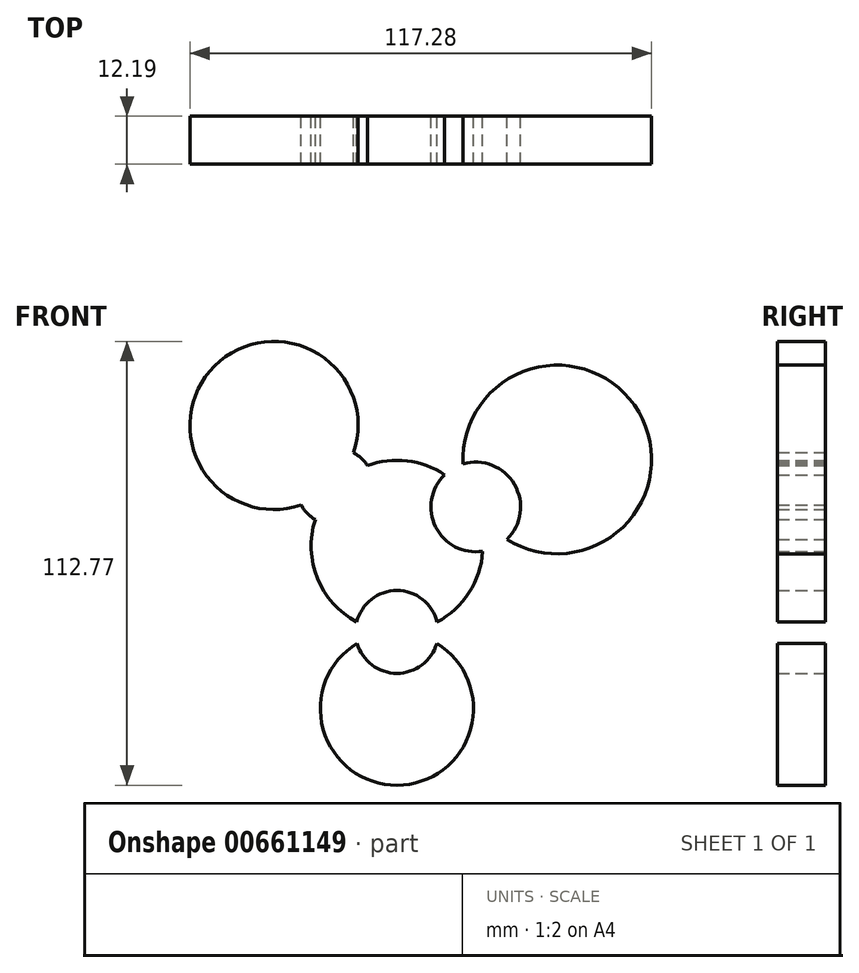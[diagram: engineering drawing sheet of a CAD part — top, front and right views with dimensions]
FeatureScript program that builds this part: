
annotation { "Feature Type Name" : "Feature", "Feature Type Description" : "" }
export const myFeature = defineFeature(function(context is Context, id is Id, definition is map)
    precondition{}
    {
        {
            var Q0;
            Q0=qCreatedBy(makeId("Front.planeOp"),FACE);
            var sketch = newSketch(context, id + "F0", { "sketchPlane" : qUnion([Q0])});
            skCircle(sketch, "E0", {"center": v(0, 0) * mm, "radius": 21.8 * mm});
            skCircle(sketch, "E1", {"center": v(-31.23, 30.65) * mm, "radius": 21.37 * mm});
            skCircle(sketch, "E2", {"center": v(40.72, 22.02) * mm, "radius": 23.96 * mm});
            skCircle(sketch, "E3", {"center": v(0, -41.3) * mm, "radius": 19.45 * mm});
            skCircle(sketch, "E4", {"center": v(-15.7, 15.13) * mm, "radius": 9.8 * mm});
            skCircle(sketch, "E5", {"center": v(20.03, 9.94) * mm, "radius": 11.38 * mm});
            skCircle(sketch, "E6", {"center": v(0, -21.8) * mm, "radius": 10.52 * mm});
            skCircle(sketch, "E7", {"center": v(-31.23, 30.65) * mm, "radius": 10.65 * mm});
            skCircle(sketch, "E8", {"center": v(40.72, 22.02) * mm, "radius": 11.28 * mm});
            skCircle(sketch, "E9", {"center": v(0, -41.3) * mm, "radius": 7.89 * mm});
            skSolve(sketch);
        }
        {
            var Q0;
            Q0=makeQuery(id+"F0.imprint","IMPRINT",FACE,{"disambiguationData":[TD([[makeQuery(id+"F0.imprint","IMPRINT",EDGE,{"derivedFrom":sQuery(id+"F0.wireOp",EDGE,"E9")}),1.0]])]});
            var Q1;
            {var subQ0=sQuery(id+"F0.wireOp",EDGE,"E6");var subQ1=sQuery(id+"F0.wireOp",EDGE,"E3");var subQ2=makeQuery(id+"F0.imprint","INTERSECT",VERTEX,{"disambiguationData":[OD(0.0)],"derivedFrom":[subQ1,subQ0]});Q1=makeQuery(id+"F0.imprint","IMPRINT",FACE,{"disambiguationData":[TD([[makeQuery(id+"F0.imprint","IMPRINT",EDGE,{"disambiguationData":[TD([[subQ2,1.0]])],"derivedFrom":subQ1}),1.0]])]});}
            var Q2;
            Q2=makeQuery(id+"F0.imprint","IMPRINT",FACE,{"disambiguationData":[TD([[makeQuery(id+"F0.imprint","IMPRINT",EDGE,{"derivedFrom":sQuery(id+"F0.wireOp",EDGE,"E8")}),1.0]])]});
            var Q3;
            Q3=makeQuery(id+"F0.imprint","IMPRINT",FACE,{"disambiguationData":[TD([[makeQuery(id+"F0.imprint","IMPRINT",EDGE,{"derivedFrom":sQuery(id+"F0.wireOp",EDGE,"E9")}),-1.0]])]});
            var Q4;
            {var subQ0=sQuery(id+"F0.wireOp",EDGE,"E6");var subQ1=sQuery(id+"F0.wireOp",EDGE,"E0");var subQ2=makeQuery(id+"F0.imprint","INTERSECT",VERTEX,{"disambiguationData":[OD(0.0)],"derivedFrom":[subQ1,subQ0]});Q4=makeQuery(id+"F0.imprint","IMPRINT",FACE,{"disambiguationData":[TD([[makeQuery(id+"F0.imprint","IMPRINT",EDGE,{"disambiguationData":[TD([[subQ2,-1.0]])],"derivedFrom":subQ1}),1.0]])]});}
            var Q5;
            {var subQ0=sQuery(id+"F0.wireOp",EDGE,"E6");var subQ1=sQuery(id+"F0.wireOp",EDGE,"E0");var subQ2=makeQuery(id+"F0.imprint","INTERSECT",VERTEX,{"disambiguationData":[OD(0.0)],"derivedFrom":[subQ1,subQ0]});Q5=makeQuery(id+"F0.imprint","IMPRINT",FACE,{"disambiguationData":[TD([[makeQuery(id+"F0.imprint","IMPRINT",EDGE,{"disambiguationData":[TD([[subQ2,-1.0]])],"derivedFrom":subQ1}),-1.0]])]});}
            var Q6;
            {var subQ0=sQuery(id+"F0.wireOp",EDGE,"E4");var subQ1=sQuery(id+"F0.wireOp",EDGE,"E0");var subQ2=makeQuery(id+"F0.imprint","INTERSECT",VERTEX,{"disambiguationData":[OD(0.0)],"derivedFrom":[subQ1,subQ0]});Q6=makeQuery(id+"F0.imprint","IMPRINT",FACE,{"disambiguationData":[TD([[makeQuery(id+"F0.imprint","IMPRINT",EDGE,{"disambiguationData":[TD([[subQ2,-1.0]])],"derivedFrom":subQ1}),1.0]])]});}
            var Q7;
            {var subQ0=sQuery(id+"F0.wireOp",EDGE,"E4");var subQ1=sQuery(id+"F0.wireOp",EDGE,"E0");var subQ2=makeQuery(id+"F0.imprint","INTERSECT",VERTEX,{"disambiguationData":[OD(0.0)],"derivedFrom":[subQ1,subQ0]});Q7=makeQuery(id+"F0.imprint","IMPRINT",FACE,{"disambiguationData":[TD([[makeQuery(id+"F0.imprint","IMPRINT",EDGE,{"disambiguationData":[TD([[subQ2,-1.0]])],"derivedFrom":subQ1}),-1.0]])]});}
            var Q8;
            Q8=makeQuery(id+"F0.imprint","IMPRINT",FACE,{"disambiguationData":[TD([[makeQuery(id+"F0.imprint","IMPRINT",EDGE,{"derivedFrom":sQuery(id+"F0.wireOp",EDGE,"E7")}),1.0]])]});
            var Q9;
            {var subQ1=sQuery(id+"F0.wireOp",EDGE,"E0");var subQ5=sQuery(id+"F0.wireOp",EDGE,"E4");var subQ6=makeQuery(id+"F0.imprint","INTERSECT",VERTEX,{"disambiguationData":[OD(0.0)],"derivedFrom":[subQ1,subQ5]});Q9=makeQuery(id+"F0.imprint","IMPRINT",FACE,{"disambiguationData":[TD([[makeQuery(id+"F0.imprint","IMPRINT",EDGE,{"disambiguationData":[TD([[subQ6,1.0]])],"derivedFrom":subQ1}),1.0]])]});}
            var Q10;
            {var subQ0=sQuery(id+"F0.wireOp",EDGE,"E5");var subQ1=sQuery(id+"F0.wireOp",EDGE,"E0");var subQ2=makeQuery(id+"F0.imprint","INTERSECT",VERTEX,{"disambiguationData":[OD(0.0)],"derivedFrom":[subQ1,subQ0]});Q10=makeQuery(id+"F0.imprint","IMPRINT",FACE,{"disambiguationData":[TD([[makeQuery(id+"F0.imprint","IMPRINT",EDGE,{"disambiguationData":[TD([[subQ2,1.0]])],"derivedFrom":subQ1}),-1.0]])]});}
            var Q11;
            {var subQ0=sQuery(id+"F0.wireOp",EDGE,"E5");var subQ1=sQuery(id+"F0.wireOp",EDGE,"E0");var subQ2=makeQuery(id+"F0.imprint","INTERSECT",VERTEX,{"disambiguationData":[OD(0.0)],"derivedFrom":[subQ1,subQ0]});Q11=makeQuery(id+"F0.imprint","IMPRINT",FACE,{"disambiguationData":[TD([[makeQuery(id+"F0.imprint","IMPRINT",EDGE,{"disambiguationData":[TD([[subQ2,1.0]])],"derivedFrom":subQ1}),1.0]])]});}
            var Q12;
            {var subQ0=sQuery(id+"F0.wireOp",EDGE,"E4");var subQ1=sQuery(id+"F0.wireOp",EDGE,"E1");var subQ2=makeQuery(id+"F0.imprint","INTERSECT",VERTEX,{"disambiguationData":[OD(0.0)],"derivedFrom":[subQ1,subQ0]});Q12=makeQuery(id+"F0.imprint","IMPRINT",FACE,{"disambiguationData":[TD([[makeQuery(id+"F0.imprint","IMPRINT",EDGE,{"disambiguationData":[TD([[subQ2,1.0]])],"derivedFrom":subQ1}),1.0]])]});}
            var Q13;
            Q13=makeQuery(id+"F0.imprint","IMPRINT",FACE,{"disambiguationData":[TD([[makeQuery(id+"F0.imprint","IMPRINT",EDGE,{"derivedFrom":sQuery(id+"F0.wireOp",EDGE,"E7")}),-1.0]])]});
            var Q14;
            {var subQ0=sQuery(id+"F0.wireOp",EDGE,"E5");var subQ1=sQuery(id+"F0.wireOp",EDGE,"E2");var subQ2=makeQuery(id+"F0.imprint","INTERSECT",VERTEX,{"disambiguationData":[OD(0.0)],"derivedFrom":[subQ1,subQ0]});Q14=makeQuery(id+"F0.imprint","IMPRINT",FACE,{"disambiguationData":[TD([[makeQuery(id+"F0.imprint","IMPRINT",EDGE,{"disambiguationData":[TD([[subQ2,-1.0]])],"derivedFrom":subQ1}),1.0]])]});}
            var Q15;
            Q15=makeQuery(id+"F0.imprint","IMPRINT",FACE,{"disambiguationData":[TD([[makeQuery(id+"F0.imprint","IMPRINT",EDGE,{"derivedFrom":sQuery(id+"F0.wireOp",EDGE,"E8")}),-1.0]])]});
            extrude(context, id + "F1", {"entities" : qUnion([Q0, Q1, Q2, Q3, Q4, Q5, Q6, Q7, Q8, Q9, Q10, Q11, Q12, Q13, Q14, Q15]), "depth" : 12.2 * mm, "offsetDistance" : 25.4 * mm});
        }
    });
